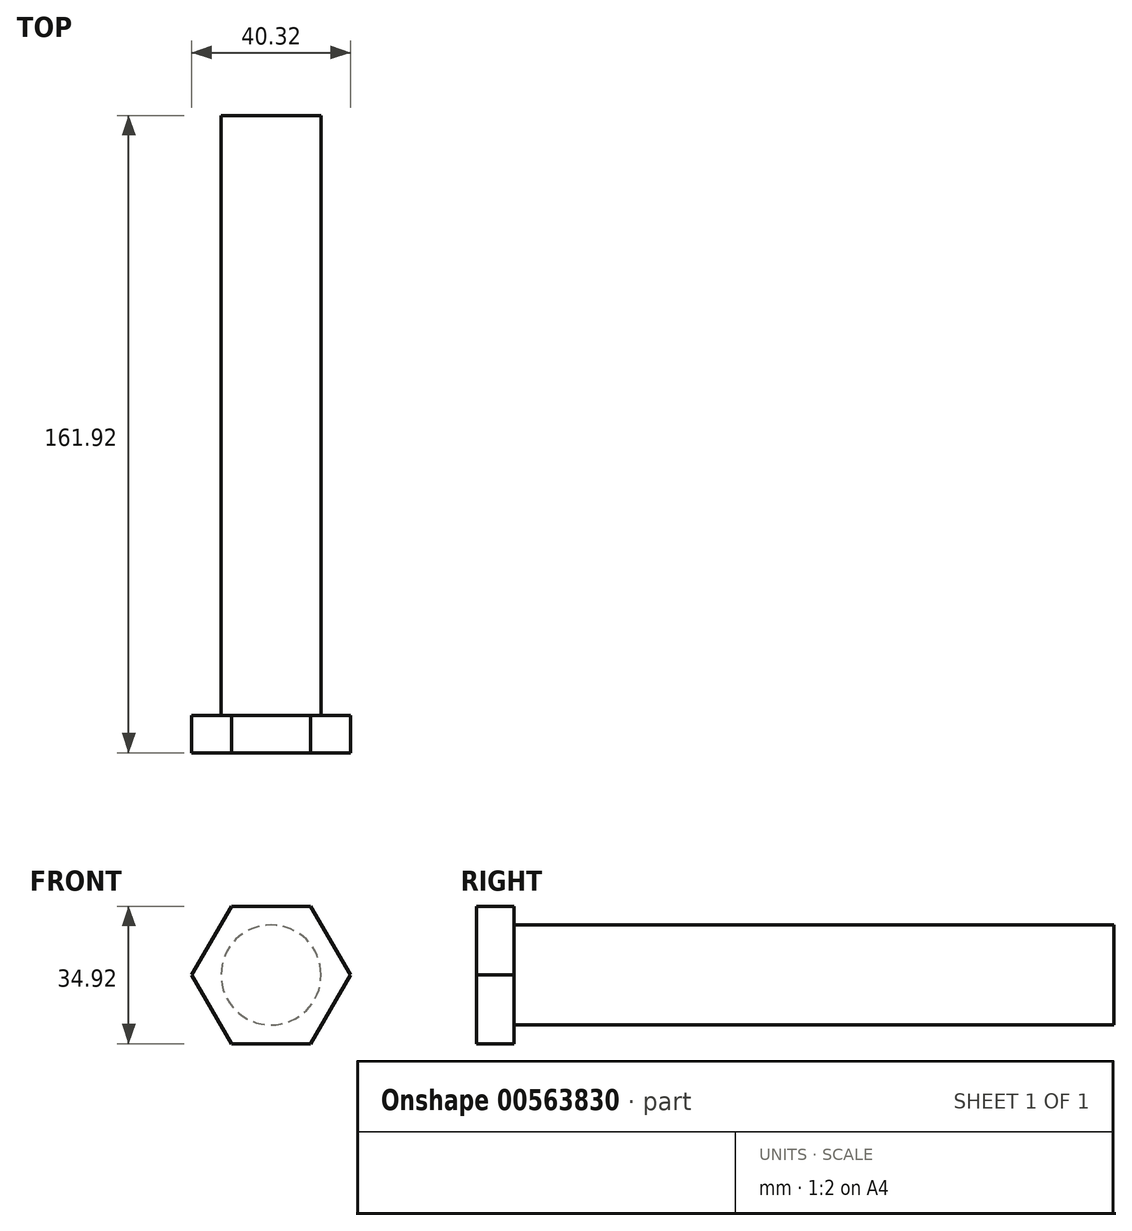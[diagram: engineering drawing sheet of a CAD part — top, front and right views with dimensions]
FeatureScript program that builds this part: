
annotation { "Feature Type Name" : "Feature", "Feature Type Description" : "" }
export const myFeature = defineFeature(function(context is Context, id is Id, definition is map)
    precondition{}
    {
        {
            var Q0;
            Q0=qCreatedBy(makeId("Front.planeOp"),FACE);
            var sketch = newSketch(context, id + "F0", { "sketchPlane" : qUnion([Q0])});
            skCircle(sketch, "E0", {"center": v(0, 0) * mm, "radius": 12.7 * mm});
            skSolve(sketch);
        }
        {
            var Q0;
            Q0=makeQuery(id+"F0.imprint","IMPRINT",FACE,{"disambiguationData":[TD([[makeQuery(id+"F0.imprint","IMPRINT",EDGE,{"derivedFrom":sQuery(id+"F0.wireOp",EDGE,"E0")}),1.0]])]});
            extrude(context, id + "F1", {"entities" : qUnion([Q0]), "endBound" : BoundingType.SYMMETRIC, "depth" : 152.4 * mm, "offsetDistance" : 25.4 * mm});
        }
        {
            var Q0;
            Q0=makeQuery(id+"F1.opExtrude","CAP_FACE",FACE,{"disambiguationData":[OSD([sQuery(id+"F0.wireOp",EDGE,"E0")])],"isStart":false});
            var sketch = newSketch(context, id + "F2", { "sketchPlane" : qUnion([Q0])});
            skCircle(sketch, "E1", {"center": v(0, 0) * mm, "radius": 17.46 * mm});
            skCircle(sketch, "E2.cCircle", {"center": v(0, 0) * mm, "radius": 17.46 * mm, "construction": true});
            skLineSegment(sketch, "E2.0", {"start": v(-10.08, 17.46) * mm, "end": v(10.08, 17.46) * mm});
            skLineSegment(sketch, "E2.1", {"start": v(10.08, 17.46) * mm, "end": v(20.16, 0) * mm});
            skLineSegment(sketch, "E2.2", {"start": v(20.16, 0) * mm, "end": v(10.08, -17.46) * mm});
            skLineSegment(sketch, "E2.3", {"start": v(10.08, -17.46) * mm, "end": v(-10.08, -17.46) * mm});
            skLineSegment(sketch, "E2.4", {"start": v(-10.08, -17.46) * mm, "end": v(-20.16, 0) * mm});
            skLineSegment(sketch, "E2.5", {"start": v(-20.16, 0) * mm, "end": v(-10.08, 17.46) * mm});
            skPoint(sketch, "E2.0.midPoint", {"position": v(0, 17.46) * mm});
            skSolve(sketch);
        }
        {
            var Q0;
            Q0=makeQuery(id+"F2.imprint","IMPRINT",FACE,{"disambiguationData":[TD([[makeQuery(id+"F2.imprint","IMPRINT",EDGE,{"derivedFrom":makeQuery(id+"F1.opExtrude","CAP_EDGE",EDGE,{"disambiguationData":[OSD([sQuery(id+"F0.wireOp",EDGE,"E0")])],"isStart":false})}),-1.0]])]});
            var Q1;
            Q1=makeQuery(id+"F2.imprint","IMPRINT",FACE,{"disambiguationData":[TD([[makeQuery(id+"F2.imprint","IMPRINT",EDGE,{"derivedFrom":makeQuery(id+"F1.opExtrude","CAP_EDGE",EDGE,{"disambiguationData":[OSD([sQuery(id+"F0.wireOp",EDGE,"E0")])],"isStart":false})}),1.0]])]});
            var Q2;
            {var subQ0=sQuery(id+"F2.wireOp",EDGE,"E2.0");var subQ1=sQuery(id+"F2.wireOp",EDGE,"E1");var subQ2=makeQuery(id+"F2.imprint","INTERSECT",VERTEX,{"derivedFrom":[subQ1,subQ0]});Q2=makeQuery(id+"F2.imprint","IMPRINT",FACE,{"disambiguationData":[TD([[makeQuery(id+"F2.imprint","IMPRINT",EDGE,{"disambiguationData":[TD([[subQ2,1.0]])],"derivedFrom":subQ1}),-1.0]])]});}
            var Q3;
            {var subQ0=sQuery(id+"F2.wireOp",EDGE,"E2.0");var subQ1=sQuery(id+"F2.wireOp",EDGE,"E1");var subQ2=makeQuery(id+"F2.imprint","INTERSECT",VERTEX,{"derivedFrom":[subQ1,subQ0]});Q3=makeQuery(id+"F2.imprint","IMPRINT",FACE,{"disambiguationData":[TD([[makeQuery(id+"F2.imprint","IMPRINT",EDGE,{"disambiguationData":[TD([[subQ2,-1.0]])],"derivedFrom":subQ1}),-1.0]])]});}
            var Q4;
            {var subQ0=sQuery(id+"F2.wireOp",EDGE,"E2.1");var subQ1=sQuery(id+"F2.wireOp",EDGE,"E1");var subQ2=makeQuery(id+"F2.imprint","INTERSECT",VERTEX,{"derivedFrom":[subQ1,subQ0]});Q4=makeQuery(id+"F2.imprint","IMPRINT",FACE,{"disambiguationData":[TD([[makeQuery(id+"F2.imprint","IMPRINT",EDGE,{"disambiguationData":[TD([[subQ2,1.0]])],"derivedFrom":subQ1}),-1.0]])]});}
            var Q5;
            {var subQ0=sQuery(id+"F2.wireOp",EDGE,"E2.3");var subQ1=sQuery(id+"F2.wireOp",EDGE,"E1");var subQ2=makeQuery(id+"F2.imprint","INTERSECT",VERTEX,{"derivedFrom":[subQ1,subQ0]});Q5=makeQuery(id+"F2.imprint","IMPRINT",FACE,{"disambiguationData":[TD([[makeQuery(id+"F2.imprint","IMPRINT",EDGE,{"disambiguationData":[TD([[subQ2,-1.0]])],"derivedFrom":subQ1}),-1.0]])]});}
            var Q6;
            {var subQ0=sQuery(id+"F2.wireOp",EDGE,"E2.4");var subQ1=sQuery(id+"F2.wireOp",EDGE,"E1");var subQ2=makeQuery(id+"F2.imprint","INTERSECT",VERTEX,{"derivedFrom":[subQ1,subQ0]});Q6=makeQuery(id+"F2.imprint","IMPRINT",FACE,{"disambiguationData":[TD([[makeQuery(id+"F2.imprint","IMPRINT",EDGE,{"disambiguationData":[TD([[subQ2,-1.0]])],"derivedFrom":subQ1}),-1.0]])]});}
            var Q7;
            {var subQ0=sQuery(id+"F2.wireOp",EDGE,"E2.5");var subQ1=sQuery(id+"F2.wireOp",EDGE,"E1");var subQ2=makeQuery(id+"F2.imprint","INTERSECT",VERTEX,{"derivedFrom":[subQ1,subQ0]});Q7=makeQuery(id+"F2.imprint","IMPRINT",FACE,{"disambiguationData":[TD([[makeQuery(id+"F2.imprint","IMPRINT",EDGE,{"disambiguationData":[TD([[subQ2,-1.0]])],"derivedFrom":subQ1}),-1.0]])]});}
            extrude(context, id + "F3", {"entities" : qUnion([Q0, Q1, Q2, Q3, Q4, Q5, Q6, Q7]), "operationType" : NewBodyOperationType.ADD, "depth" : 9.52 * mm, "offsetDistance" : 25.4 * mm});
        }
    });
